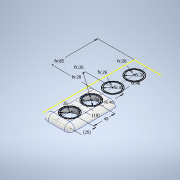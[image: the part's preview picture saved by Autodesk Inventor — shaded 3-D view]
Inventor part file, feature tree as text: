
AUTODESK INVENTOR PART (.ipt)
format: ipt  version: 2021 (Build 250183000, 183)  size: 1,556,992 bytes
history: native  units: in
note: dims shown in document units (in); Inventor stores cm internally (conversion verified against a paired STEP export)
features: extrude x11, other x7, fillet x2, sketch x2
ambient origin geometry x8: Origin, YZ Plane, XZ Plane, XY Plane, X Axis, Y Axis, Z Axis, Center Point
bodies: Body1 (feature_tree)
feature tree (22):
  extrude  "Base"  Depth=1.9685in
  other  "Top Sketch"
  extrude  "Top"  Depth=1.1811in
  extrude  "Walls"  Depth=1.1811in
  fillet  "Outer"  Radius=1.1811in
  extrude  "Wire"  Depth=1.1811in
  extrude  "Wall Holes"  Depth=1.5748in
  extrude  "Text"  Depth=1.5748in
  extrude  "Extrusion9"  Depth=1.5748in
  fillet  "Inner Fillet"  Radius=0.7087in
  extrude  "Extrusion14"  Depth=0.315in
  extrude  "Extrusion16"  Depth=0.315in
  extrude  "Extrusion17"  Depth=0.2362in
  extrude  "Extrusion18"  Depth=0.2362in
  other  "Base Sketch"
  other  "Walls Sketch"
  other  "Wire Sketch"
  other  "Wall Holes Sketch"
  other  "Text Sketch"
  other  "Support"
  sketch  "Sketch25"  dims[d6=6.6929in d7=1.9685in]
  sketch  "Sketch26"  dims[d8=1.7717in d9=0.0in d10=1.1811in d11=1.1811in d12=1.1811in d13=1.1811in d14=1.5748in d15=1.5748in d16=1.5748in d19=0.7087in d20=0.0in d21=0.315in d22=0.315in d23=0.2362in d24=0.2362in d25=1.378in d26=0.0in d27=1.0236in d28=1.0236in d29=1.0236in d30=1.0236in d31=0.7874in d32=3.3465in d33=1.4961in d35=0.9843in d36=0.3937in d38=0.3937in d39=0.0in d52=0.315in d55=0.1969in d56=0.0in d58=0.3937in d65=0.315in d66=0.1575in d67=0.1575in d68=0.315in d69=0.2774in d70=0.2774in d71=0.0499in d72=0.0499in d73=1.6535in d74=0.0in d77=0.6496in d81=0.5906in d82=0.0in d85=0.4724in d86=0.1575in d87=0.1575in d88=0.9843in d89=0.315in d90=0.1575in d92=0.0in d93=0.1181in d94=0.0in d95=0.1575in d96=0.6496in d131=0.1969in d132=0.0in d143=0.0in d144=0.0in d145=0.1969in d146=0.1969in d151=0.2756in d152=0.0in d153=0.2756in d154=0.0in d155=3.3465in d156=0.0in d157=0.1969in d158=0.0709in d159=0.0in d160=1.378in d161=0.0in d44=0.0197in d45=0.0344in d46=0.0197in d47=0.0344in d48=0.0197in d49=0.0344in d59=0.0197in d60=0.0344in d61=0.0197in d62=0.0344in]
